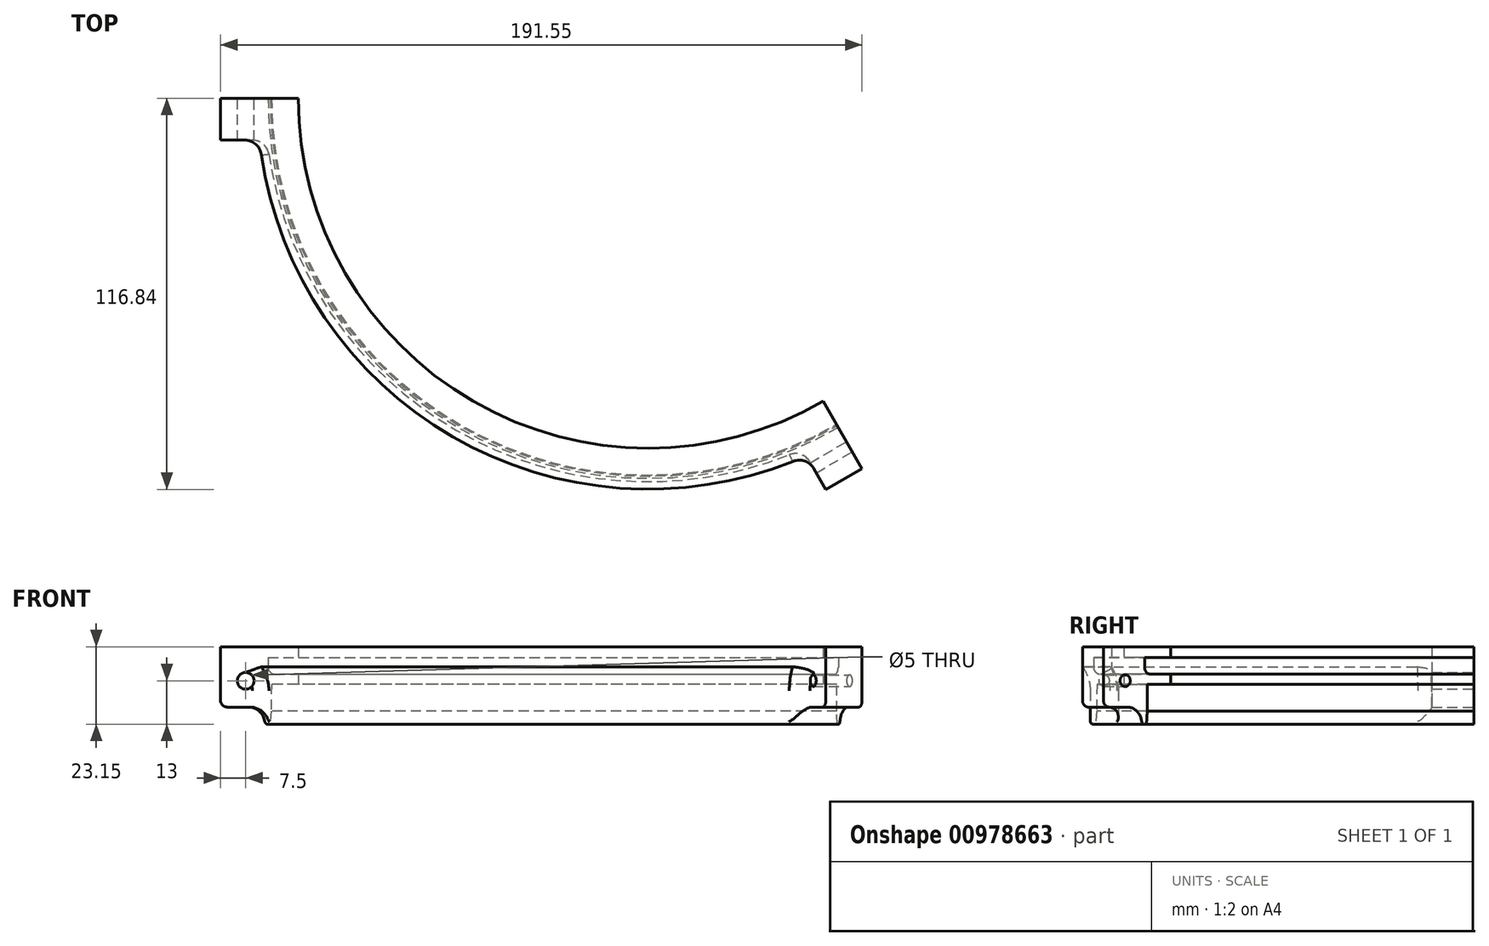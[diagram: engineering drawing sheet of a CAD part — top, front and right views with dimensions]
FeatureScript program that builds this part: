
annotation { "Feature Type Name" : "Feature", "Feature Type Description" : "" }
export const myFeature = defineFeature(function(context is Context, id is Id, definition is map)
    precondition{}
    {
        {
            var Q0;
            Q0=qCreatedBy(makeId("Front.planeOp"),FACE);
            var sketch = newSketch(context, id + "F0", { "sketchPlane" : qUnion([Q0])});
            skLineSegment(sketch, "E0", {"start": v(0, 0) * mm, "end": v(-112.5, 0) * mm});
            skLineSegment(sketch, "E1", {"start": v(-104.5, -3) * mm, "end": v(-112.5, -3) * mm});
            skLineSegment(sketch, "E2", {"start": v(-105.25, 8.15) * mm, "end": v(-116.75, 8.15) * mm});
            skLineSegment(sketch, "E3", {"start": v(-114.5, -15) * mm, "end": v(-114.5, -5) * mm});
            skLineSegment(sketch, "E4", {"start": v(-116.75, 8.15) * mm, "end": v(-116.75, 2.15) * mm});
            skLineSegment(sketch, "E5", {"start": v(0, -15.27) * mm, "end": v(0, 14.73) * mm});
            skLineSegment(sketch, "E6", {"start": v(-104.5, -3) * mm, "end": v(-104.5, 8.15) * mm});
            skLineSegment(sketch, "E7", {"start": v(-105.25, 8.15) * mm, "end": v(-104.5, 8.15) * mm});
            skArc(sketch, "E8", {"start": v(-114.5, -5) * mm, "mid": v(-115.08, -1.25) * mm, "end": v(-116.75, 2.15) * mm});
            skLineSegment(sketch, "E9", {"start": v(-114.5, -15) * mm, "end": v(-112.9, -15) * mm});
            skLineSegment(sketch, "E10", {"start": v(-112.5, -3) * mm, "end": v(-112.64, -11) * mm});
            skLineSegment(sketch, "E11", {"start": v(-112.64, -11) * mm, "end": v(-112.9, -15) * mm});
            skSolve(sketch);
        }
        {
            var Q0;
            Q0=qSketchRegion(id+"F0",true);
            var Q1;
            Q1=sQuery(id+"F0.wireOp",EDGE,"E5");
            revolve(context, id + "F1", {"surfaceOperationType" : NewSurfaceOperationType.NEW, "entities" : qUnion([Q0]), "axis" : qUnion([Q1]), "revolveType" : RevolveType.FULL});
        }
        {
            var Q0;
            Q0=qCreatedBy(makeId("Top.planeOp"),FACE);
            var sketch = newSketch(context, id + "F2", { "sketchPlane" : qUnion([Q0])});
            skCircle(sketch, "E12", {"center": v(0, 0) * mm, "radius": 113.5 * mm});
            skSolve(sketch);
        }
        {
            var Q0;
            Q0=qSketchRegion(id+"F2",true);
            extrude(context, id + "F3", {"entities" : qUnion([Q0]), "operationType" : NewBodyOperationType.REMOVE, "depth" : 5 * mm, "offsetDistance" : 25 * mm});
        }
        {
            var Q0;
            Q0=makeQuery(id+"F1.opRevolve","SWEPT_EDGE",EDGE,{"disambiguationData":[OSD([sQuery(id+"F0.wireOp",EDGE,"gYxMhwdu-58K6-m69u-6tx5-LIJCVqVKQSf0"),sQuery(id+"F0.wireOp",EDGE,"E3")])]});
            fillet(context, id + "F4", {"entities" : qUnion([Q0]), "radius" : 1 * mm, "tangentPropagation" : true, "allowEdgeOverflow" : false});
        }
        {
            var Q0;
            Q0=qCreatedBy(makeId("Front.planeOp"),FACE);
            var sketch = newSketch(context, id + "F5", { "sketchPlane" : qUnion([Q0])});
            skLineSegment(sketch, "E13.bottom", {"start": v(-113.7, 8.15) * mm, "end": v(-127.7, 8.15) * mm});
            skLineSegment(sketch, "E13.top", {"start": v(-113.7, -9.85) * mm, "end": v(-127.7, -9.85) * mm});
            skLineSegment(sketch, "E13.left", {"start": v(-113.7, 8.15) * mm, "end": v(-113.7, -9.85) * mm});
            skLineSegment(sketch, "E13.right", {"start": v(-127.7, 8.15) * mm, "end": v(-127.7, -9.85) * mm});
            skCircle(sketch, "E14", {"center": v(-120.2, -2) * mm, "radius": 2.5 * mm});
            skSolve(sketch);
        }
        {
            var Q0;
            Q0=qCreatedBy(makeId("Front.planeOp"),FACE);
            var sketch = newSketch(context, id + "F6", { "sketchPlane" : qUnion([Q0])});
            skLineSegment(sketch, "E15.bottom", {"start": v(127.7, 8.1) * mm, "end": v(113.7, 8.1) * mm});
            skLineSegment(sketch, "E15.top", {"start": v(127.7, -9.9) * mm, "end": v(113.7, -9.9) * mm});
            skLineSegment(sketch, "E15.left", {"start": v(127.7, 8.1) * mm, "end": v(127.7, -9.9) * mm});
            skLineSegment(sketch, "E15.right", {"start": v(113.7, 8.1) * mm, "end": v(113.7, -9.9) * mm});
            skCircle(sketch, "E16", {"center": v(120.2, -2) * mm, "radius": 1.75 * mm});
            skSolve(sketch);
        }
        {
            var Q0;
            Q0=qSketchRegion(id+"F5",true);
            extrude(context, id + "F7", {"entities" : qUnion([Q0]), "operationType" : NewBodyOperationType.ADD, "endBound" : BoundingType.SYMMETRIC, "depth" : 25 * mm, "offsetDistance" : 25 * mm});
        }
        {
            var Q0;
            Q0=qSketchRegion(id+"F6",true);
            extrude(context, id + "F8", {"entities" : qUnion([Q0]), "operationType" : NewBodyOperationType.ADD, "endBound" : BoundingType.SYMMETRIC, "depth" : 25 * mm, "offsetDistance" : 25 * mm});
        }
        {
            var Q0;
            Q0=qCreatedBy(makeId("Front.planeOp"),FACE);
            var sketch = newSketch(context, id + "F9", { "sketchPlane" : qUnion([Q0])});
            skLineSegment(sketch, "E17.bottom", {"start": v(-164.88, 17.7) * mm, "end": v(135.12, 17.7) * mm});
            skLineSegment(sketch, "E17.top", {"start": v(-164.88, -82.3) * mm, "end": v(135.12, -82.3) * mm});
            skLineSegment(sketch, "E17.left", {"start": v(-164.88, 17.7) * mm, "end": v(-164.88, -82.3) * mm});
            skLineSegment(sketch, "E17.right", {"start": v(135.12, 17.7) * mm, "end": v(135.12, -82.3) * mm});
            skSolve(sketch);
        }
        {
            var Q0;
            Q0=qSketchRegion(id+"F9",true);
            extrude(context, id + "F10", {"entities" : qUnion([Q0]), "operationType" : NewBodyOperationType.REMOVE, "oppositeDirection" : true, "depth" : 150 * mm, "offsetDistance" : 25 * mm});
        }
        {
            var Q0;
            Q0=makeQuery(id+"F10.boolean.opBoolean","COPY",FACE,{"disambiguationData":[TD([makeQuery(id+"F8.opExtrude","SWEPT_FACE",FACE,{"disambiguationData":[OSD([sQuery(id+"F6.wireOp",EDGE,"E15.bottom")])]})])],"derivedFrom":makeQuery(id+"F10.opExtrude","CAP_FACE",FACE,{"disambiguationData":[OSD([sQuery(id+"F9.wireOp",EDGE,"E17.bottom"),sQuery(id+"F9.wireOp",EDGE,"E17.top"),sQuery(id+"F9.wireOp",EDGE,"E17.left"),sQuery(id+"F9.wireOp",EDGE,"E17.right")])],"isStart":true})});
            var Q1;
            Q1=makeQuery(id+"F1.opRevolve","SWEPT_EDGE",EDGE,{"disambiguationData":[OSD([sQuery(id+"F0.wireOp",EDGE,"E2"),sQuery(id+"F0.wireOp",EDGE,"E4")])]});
            cPlane(context, id + "F11", {"entities" : qUnion([Q0, Q1]), "cplaneType" : CPlaneType.LINE_ANGLE, "offset" : 25 * mm, "angle" : 60 * degree, "width" : 150 * mm, "height" : 150 * mm});
        }
        {
            var Q0;
            Q0=qCreatedBy(id+"F11.planeOp",FACE);
            var sketch = newSketch(context, id + "F12", { "sketchPlane" : qUnion([Q0])});
            skLineSegment(sketch, "E18.bottom", {"start": v(127.7, 8.15) * mm, "end": v(113.7, 8.15) * mm});
            skLineSegment(sketch, "E18.top", {"start": v(127.7, -9.85) * mm, "end": v(113.7, -9.85) * mm});
            skLineSegment(sketch, "E18.left", {"start": v(127.7, 8.15) * mm, "end": v(127.7, -9.85) * mm});
            skLineSegment(sketch, "E18.right", {"start": v(113.7, 8.15) * mm, "end": v(113.7, -9.85) * mm});
            skCircle(sketch, "E19", {"center": v(120.2, -1.95) * mm, "radius": 1.75 * mm});
            skSolve(sketch);
        }
        {
            var Q0;
            Q0 = qSketchRegion(id + "F12", true);
            extrude(context, id + "F13", {"entities" : qUnion([Q0]), "operationType" : NewBodyOperationType.ADD, "endBound" : BoundingType.SYMMETRIC, "depth" : 25 * mm, "offsetDistance" : 25 * mm});
        }
        {
            var Q0;
            Q0=makeQuery(id+"F3.boolean.opBoolean","COPY",EDGE,{"derivedFrom":makeQuery(id+"F3.opExtrude","CAP_EDGE",EDGE,{"disambiguationData":[OSD([sQuery(id+"F2.wireOp",EDGE,"E12")])],"isStart":true})});
            fillet(context, id + "F14", {"entities" : qUnion([Q0]), "radius" : 2 * mm, "tangentPropagation" : true, "allowEdgeOverflow" : false});
        }
        {
            var Q0;
            Q0=makeQuery(id+"F8.opExtrude","SWEPT_EDGE",EDGE,{"disambiguationData":[OSD([sQuery(id+"F6.wireOp",EDGE,"E15.top"),sQuery(id+"F6.wireOp",EDGE,"E15.left")])]});
            var Q1;
            Q1=makeQuery(id+"F7.opExtrude","SWEPT_EDGE",EDGE,{"disambiguationData":[OSD([sQuery(id+"F5.wireOp",EDGE,"E13.top"),sQuery(id+"F5.wireOp",EDGE,"E13.right")])]});
            var Q2;
            Q2=makeQuery(id+"F13.opExtrude","SWEPT_EDGE",EDGE,{"disambiguationData":[OSD([sQuery(id+"F12.wireOp",EDGE,"E18.top"),sQuery(id+"F12.wireOp",EDGE,"E18.left")])]});
            fillet(context, id + "F15", {"entities" : qUnion([Q0, Q1, Q2]), "radius" : 2 * mm, "tangentPropagation" : true, "allowEdgeOverflow" : false});
        }
        {
            var Q0;
            Q0=qCreatedBy(id+"F11.planeOp",FACE);
            var sketch = newSketch(context, id + "F16", { "sketchPlane" : qUnion([Q0])});
            skLineSegment(sketch, "E20.bottom", {"start": v(-177.45, 38.96) * mm, "end": v(266.58, 38.96) * mm});
            skLineSegment(sketch, "E20.top", {"start": v(-177.45, -98.64) * mm, "end": v(266.58, -98.64) * mm});
            skLineSegment(sketch, "E20.left", {"start": v(-177.45, 38.96) * mm, "end": v(-177.45, -98.64) * mm});
            skLineSegment(sketch, "E20.right", {"start": v(266.58, 38.96) * mm, "end": v(266.58, -98.64) * mm});
            skSolve(sketch);
        }
        {
            var Q0;
            Q0 = qSketchRegion(id + "F16", true);
            extrude(context, id + "F17", {"entities" : qUnion([Q0]), "operationType" : NewBodyOperationType.REMOVE, "oppositeDirection" : true, "depth" : 150 * mm, "offsetDistance" : 25 * mm});
        }
        {
            var Q0;
            Q0=makeQuery(id+"F7.boolean.opBoolean","INTERSECT",EDGE,{"derivedFrom":[makeQuery(id+"F1.opRevolve","SWEPT_FACE",FACE,{"disambiguationData":[OSD([sQuery(id+"F0.wireOp",EDGE,"E8")])]}),makeQuery(id+"F7.opExtrude","CAP_FACE",FACE,{"disambiguationData":[OSD([sQuery(id+"F5.wireOp",EDGE,"E13.bottom"),sQuery(id+"F5.wireOp",EDGE,"E13.top"),sQuery(id+"F5.wireOp",EDGE,"E13.left"),sQuery(id+"F5.wireOp",EDGE,"E13.right"),sQuery(id+"F5.wireOp",EDGE,"E14")])],"isStart":false})]});
            var Q1;
            Q1=makeQuery(id+"F7.boolean.opBoolean","INTERSECT",EDGE,{"derivedFrom":[makeQuery(id+"F1.opRevolve","SWEPT_FACE",FACE,{"disambiguationData":[OSD([sQuery(id+"F0.wireOp",EDGE,"E4")])]}),makeQuery(id+"F7.opExtrude","CAP_FACE",FACE,{"disambiguationData":[OSD([sQuery(id+"F5.wireOp",EDGE,"E13.bottom"),sQuery(id+"F5.wireOp",EDGE,"E13.top"),sQuery(id+"F5.wireOp",EDGE,"E13.left"),sQuery(id+"F5.wireOp",EDGE,"E13.right"),sQuery(id+"F5.wireOp",EDGE,"E14")])],"isStart":false})]});
            var Q2;
            Q2=makeQuery(id+"F7.boolean.opBoolean","INTERSECT",EDGE,{"derivedFrom":[makeQuery(id+"F1.opRevolve","SWEPT_FACE",FACE,{"disambiguationData":[OSD([sQuery(id+"F0.wireOp",EDGE,"E3")])]}),makeQuery(id+"F7.opExtrude","CAP_FACE",FACE,{"disambiguationData":[OSD([sQuery(id+"F5.wireOp",EDGE,"E13.bottom"),sQuery(id+"F5.wireOp",EDGE,"E13.top"),sQuery(id+"F5.wireOp",EDGE,"E13.left"),sQuery(id+"F5.wireOp",EDGE,"E13.right"),sQuery(id+"F5.wireOp",EDGE,"E14")])],"isStart":false})]});
            var Q3;
            Q3=makeQuery(id+"F7.boolean.opBoolean","INTERSECT",EDGE,{"derivedFrom":[makeQuery(id+"F1.opRevolve","SWEPT_FACE",FACE,{"disambiguationData":[OSD([sQuery(id+"F0.wireOp",EDGE,"E3")])]}),makeQuery(id+"F7.opExtrude","SWEPT_FACE",FACE,{"disambiguationData":[OSD([sQuery(id+"F5.wireOp",EDGE,"E13.top")])]})]});
            fillet(context, id + "F18", {"entities" : qUnion([Q0, Q1, Q2, Q3]), "radius" : 5 * mm, "tangentPropagation" : true, "allowEdgeOverflow" : false});
        }
        {
            var Q0;
            Q0=makeQuery(id+"F13.boolean.opBoolean","INTERSECT",EDGE,{"derivedFrom":[makeQuery(id+"F1.opRevolve","SWEPT_FACE",FACE,{"disambiguationData":[OSD([sQuery(id+"F0.wireOp",EDGE,"E4")])]}),makeQuery(id+"F13.opExtrude","CAP_FACE",FACE,{"disambiguationData":[OSD([sQuery(id+"F12.wireOp",EDGE,"E18.bottom"),sQuery(id+"F12.wireOp",EDGE,"E18.top"),sQuery(id+"F12.wireOp",EDGE,"E18.left"),sQuery(id+"F12.wireOp",EDGE,"E18.right"),sQuery(id+"F12.wireOp",EDGE,"E19")])],"isStart":false})]});
            var Q1;
            Q1=makeQuery(id+"F13.boolean.opBoolean","INTERSECT",EDGE,{"derivedFrom":[makeQuery(id+"F8.boolean.opBoolean","SPLIT",FACE,{"disambiguationData":[TD([makeQuery(id+"F7.opExtrude","CAP_FACE",FACE,{"disambiguationData":[OSD([sQuery(id+"F5.wireOp",EDGE,"E13.bottom"),sQuery(id+"F5.wireOp",EDGE,"E13.top"),sQuery(id+"F5.wireOp",EDGE,"E13.left"),sQuery(id+"F5.wireOp",EDGE,"E13.right"),sQuery(id+"F5.wireOp",EDGE,"E14")])],"isStart":false})])],"derivedFrom":makeQuery(id+"F1.opRevolve","SWEPT_FACE",FACE,{"disambiguationData":[OSD([sQuery(id+"F0.wireOp",EDGE,"E8")])]})}),makeQuery(id+"F13.opExtrude","CAP_FACE",FACE,{"disambiguationData":[OSD([sQuery(id+"F12.wireOp",EDGE,"E18.bottom"),sQuery(id+"F12.wireOp",EDGE,"E18.top"),sQuery(id+"F12.wireOp",EDGE,"E18.left"),sQuery(id+"F12.wireOp",EDGE,"E18.right"),sQuery(id+"F12.wireOp",EDGE,"E19")])],"isStart":false})]});
            var Q2;
            Q2=makeQuery(id+"F13.boolean.opBoolean","INTERSECT",EDGE,{"derivedFrom":[makeQuery(id+"F1.opRevolve","SWEPT_FACE",FACE,{"disambiguationData":[OSD([sQuery(id+"F0.wireOp",EDGE,"E3")])]}),makeQuery(id+"F13.opExtrude","CAP_FACE",FACE,{"disambiguationData":[OSD([sQuery(id+"F12.wireOp",EDGE,"E18.bottom"),sQuery(id+"F12.wireOp",EDGE,"E18.top"),sQuery(id+"F12.wireOp",EDGE,"E18.left"),sQuery(id+"F12.wireOp",EDGE,"E18.right"),sQuery(id+"F12.wireOp",EDGE,"E19")])],"isStart":false})]});
            var Q3;
            Q3=makeQuery(id+"F13.boolean.opBoolean","INTERSECT",EDGE,{"derivedFrom":[makeQuery(id+"F1.opRevolve","SWEPT_FACE",FACE,{"disambiguationData":[OSD([sQuery(id+"F0.wireOp",EDGE,"E3")])]}),makeQuery(id+"F13.opExtrude","SWEPT_FACE",FACE,{"disambiguationData":[OSD([sQuery(id+"F12.wireOp",EDGE,"E18.top")])]})]});
            fillet(context, id + "F19", {"entities" : qUnion([Q0, Q1, Q2, Q3]), "radius" : 5 * mm, "tangentPropagation" : true, "allowEdgeOverflow" : false});
        }
    });
